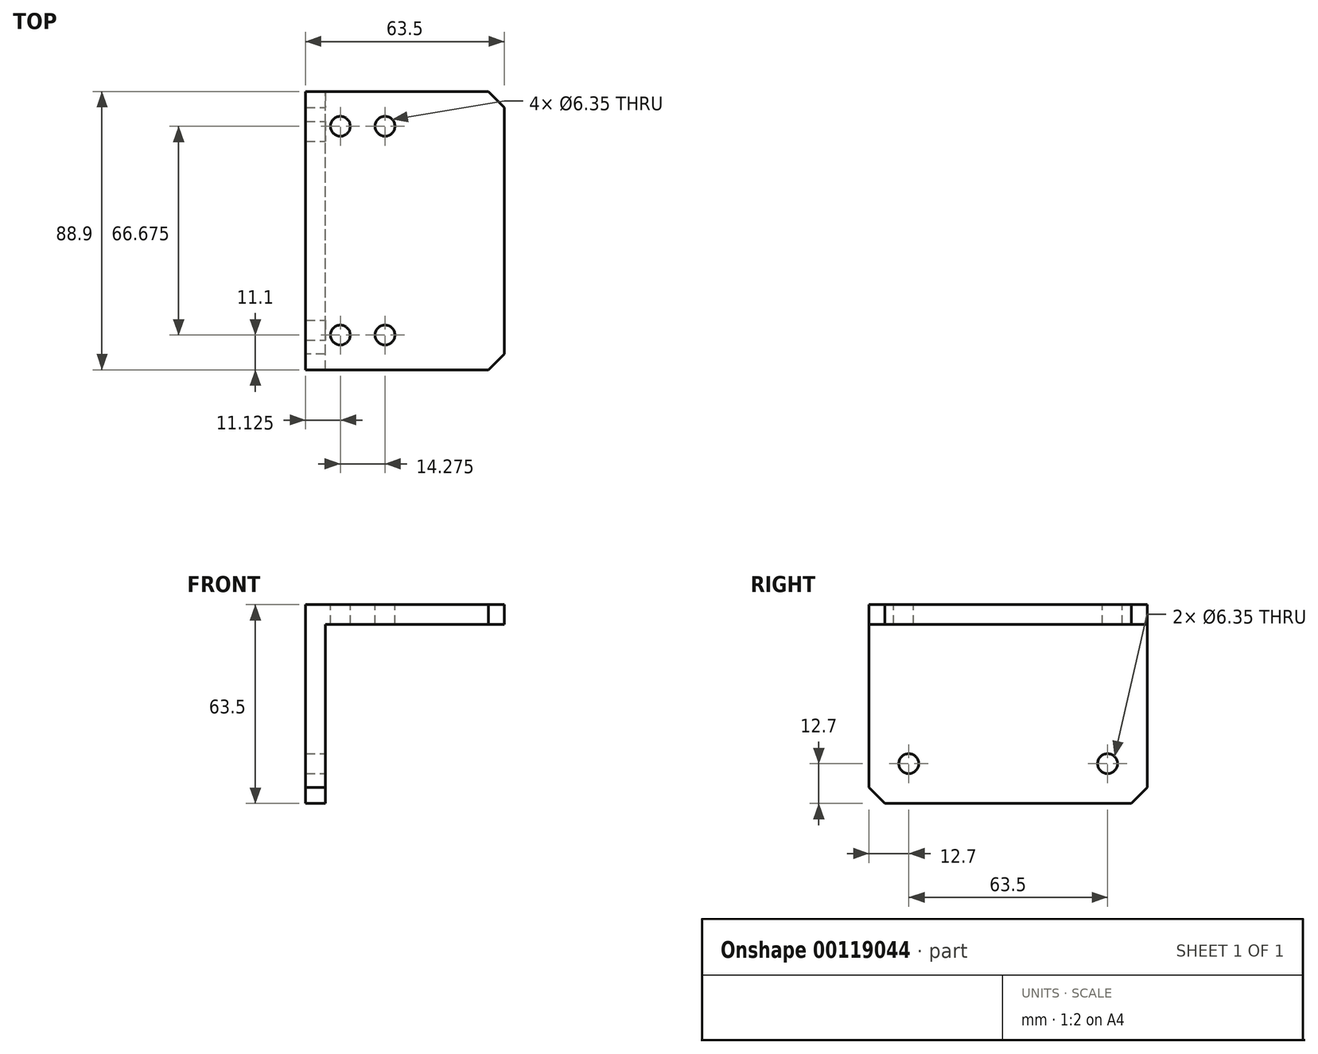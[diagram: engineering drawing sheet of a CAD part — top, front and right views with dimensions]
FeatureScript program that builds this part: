
annotation { "Feature Type Name" : "Feature", "Feature Type Description" : "" }
export const myFeature = defineFeature(function(context is Context, id is Id, definition is map)
    precondition{}
    {
        {
            var Q0;
            Q0=qCreatedBy(makeId("Front.planeOp"),FACE);
            var sketch = newSketch(context, id + "F0", { "sketchPlane" : qUnion([Q0])});
            skLineSegment(sketch, "E0", {"start": v(0, 0) * mm, "end": v(6.35, 0) * mm});
            skLineSegment(sketch, "E1", {"start": v(0, 0) * mm, "end": v(0, 63.5) * mm});
            skLineSegment(sketch, "E2", {"start": v(0, 63.5) * mm, "end": v(63.5, 63.5) * mm});
            skLineSegment(sketch, "E3", {"start": v(63.5, 63.5) * mm, "end": v(63.5, 57.15) * mm});
            skLineSegment(sketch, "E4", {"start": v(63.5, 57.15) * mm, "end": v(6.35, 57.15) * mm});
            skLineSegment(sketch, "E5", {"start": v(6.35, 0) * mm, "end": v(6.35, 57.15) * mm});
            skSolve(sketch);
        }
        {
            var Q0;
            Q0 = qSketchRegion(id + "F0", true);
            extrude(context, id + "F1", {"entities" : qUnion([Q0]), "depth" : 88.9 * mm});
        }
        {
            var Q0;
            Q0=makeQuery(id+"F1.opExtrude","SWEPT_FACE",FACE,{"disambiguationData":[OSD([sQuery(id+"F0.wireOp",EDGE,"E5")])]});
            var sketch = newSketch(context, id + "F2", { "sketchPlane" : qUnion([Q0])});
            skPoint(sketch, "E6", {"position": v(-76.2, 12.7) * mm});
            skPoint(sketch, "E7", {"position": v(-12.7, 12.7) * mm});
            skSolve(sketch);
        }
        {
            var Q0;
            Q0=sQuery(id+"F2.wireOp",VERTEX,"E6");
            var Q1;
            Q1=sQuery(id+"F2.wireOp",VERTEX,"E7");
            var Q2;
            Q2=makeQuery(id+"F1.opExtrude","SWEPT_BODY",BODY,{"disambiguationData":[OSD([sQuery(id+"F0.wireOp",EDGE,"E0"),sQuery(id+"F0.wireOp",EDGE,"E1"),sQuery(id+"F0.wireOp",EDGE,"E2"),sQuery(id+"F0.wireOp",EDGE,"E3"),sQuery(id+"F0.wireOp",EDGE,"E4"),sQuery(id+"F0.wireOp",EDGE,"E5")])]});
            hole(context, id + "F3", {"style" : HoleStyle.SIMPLE, "endStyle" : HoleEndStyle.THROUGH, "holeDiameter" : 6.35 * mm, "locations" : qUnion([Q0, Q1]), "scope" : qUnion([Q2]), "isTappedThrough" : true});
        }
        {
            var Q0;
            Q0=makeQuery(id+"F1.opExtrude","CAP_EDGE",EDGE,{"disambiguationData":[OSD([sQuery(id+"F0.wireOp",EDGE,"E0")])],"isStart":false});
            var Q1;
            Q1=makeQuery(id+"F1.opExtrude","CAP_EDGE",EDGE,{"disambiguationData":[OSD([sQuery(id+"F0.wireOp",EDGE,"E0")])],"isStart":true});
            var Q2;
            Q2=makeQuery(id+"F1.opExtrude","CAP_EDGE",EDGE,{"disambiguationData":[OSD([sQuery(id+"F0.wireOp",EDGE,"E3")])],"isStart":false});
            var Q3;
            Q3=makeQuery(id+"F1.opExtrude","CAP_EDGE",EDGE,{"disambiguationData":[OSD([sQuery(id+"F0.wireOp",EDGE,"E3")])],"isStart":true});
            chamfer(context, id + "F4", {"entities" : qUnion([Q0, Q1, Q2, Q3]), "width" : 5.08 * mm, "tangentPropagation" : true});
        }
        {
            var Q0;
            Q0=makeQuery(id+"F1.opExtrude","SWEPT_FACE",FACE,{"disambiguationData":[OSD([sQuery(id+"F0.wireOp",EDGE,"E2")])]});
            var sketch = newSketch(context, id + "F5", { "sketchPlane" : qUnion([Q0])});
            skPoint(sketch, "E8", {"position": v(25.4, -11.13) * mm});
            skPoint(sketch, "E9", {"position": v(11.13, -11.13) * mm});
            skPoint(sketch, "E10", {"position": v(11.13, -77.8) * mm});
            skPoint(sketch, "E11", {"position": v(25.4, -77.8) * mm});
            skSolve(sketch);
        }
        {
            var Q0;
            Q0=sQuery(id+"F5.wireOp",VERTEX,"E8");
            var Q1;
            Q1=sQuery(id+"F5.wireOp",VERTEX,"E9");
            var Q2;
            Q2=sQuery(id+"F5.wireOp",VERTEX,"E10");
            var Q3;
            Q3=sQuery(id+"F5.wireOp",VERTEX,"E11");
            var Q4;
            Q4=makeQuery(id+"F1.opExtrude","SWEPT_BODY",BODY,{"disambiguationData":[OSD([sQuery(id+"F0.wireOp",EDGE,"E0"),sQuery(id+"F0.wireOp",EDGE,"E1"),sQuery(id+"F0.wireOp",EDGE,"E2"),sQuery(id+"F0.wireOp",EDGE,"E3"),sQuery(id+"F0.wireOp",EDGE,"E4"),sQuery(id+"F0.wireOp",EDGE,"E5")])]});
            hole(context, id + "F6", {"style" : HoleStyle.SIMPLE, "endStyle" : HoleEndStyle.THROUGH, "holeDiameter" : 6.35 * mm, "locations" : qUnion([Q0, Q1, Q2, Q3]), "scope" : qUnion([Q4]), "isTappedThrough" : true});
        }
    });
